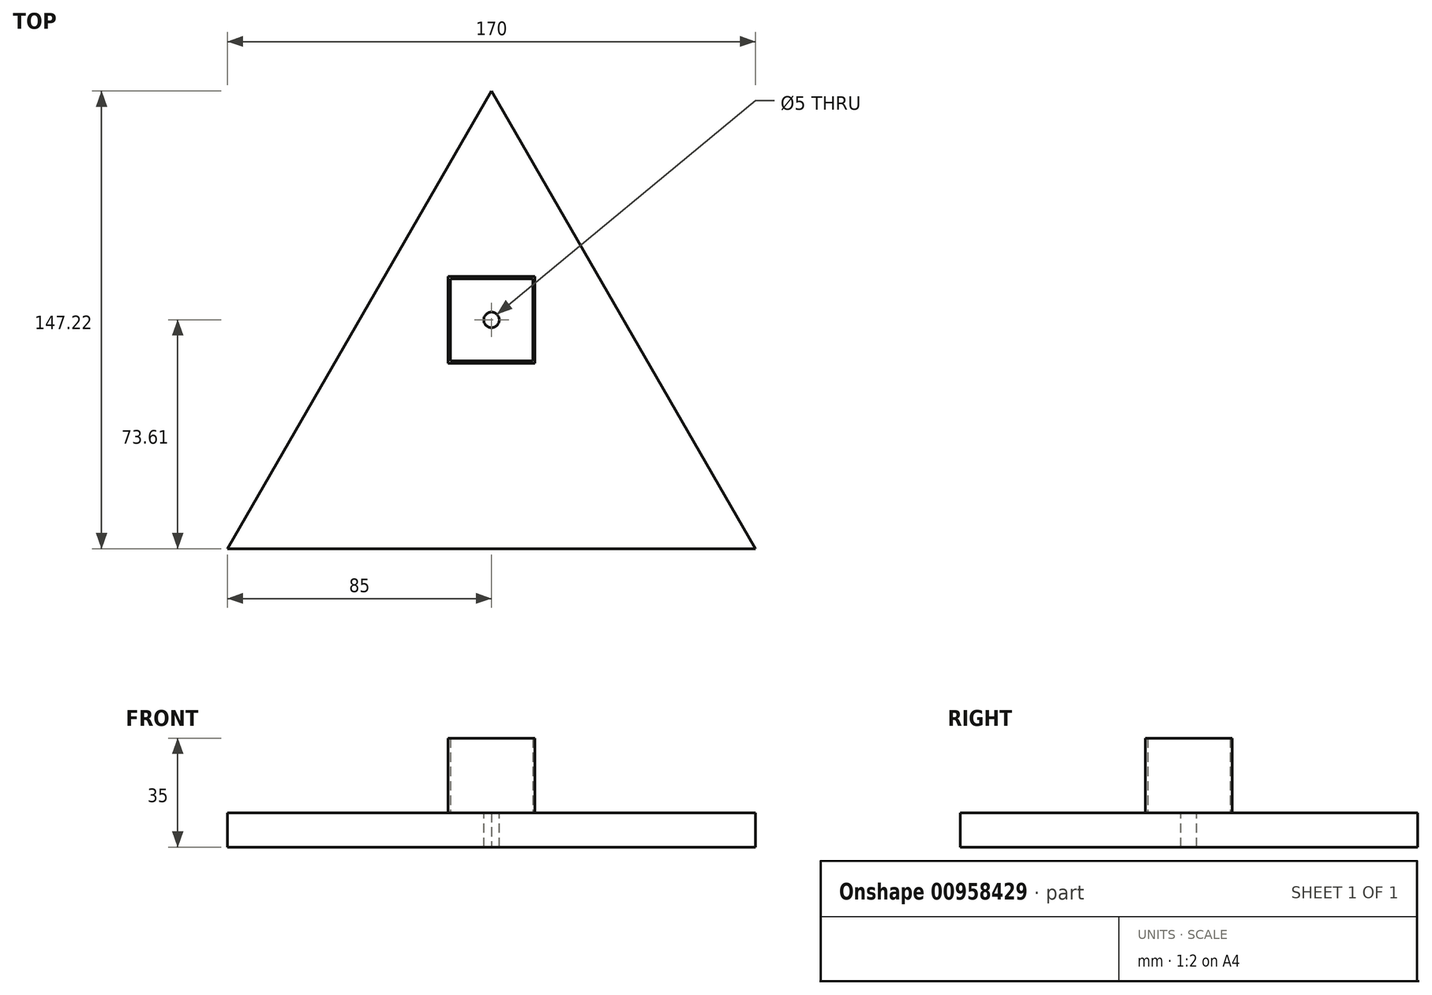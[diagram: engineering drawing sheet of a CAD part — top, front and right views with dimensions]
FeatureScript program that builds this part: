
annotation { "Feature Type Name" : "Feature", "Feature Type Description" : "" }
export const myFeature = defineFeature(function(context is Context, id is Id, definition is map)
    precondition{}
    {
        {
            var Q0;
            Q0=qCreatedBy(makeId("Top.planeOp"),FACE);
            var sketch = newSketch(context, id + "F0", { "sketchPlane" : qUnion([Q0])});
            skLineSegment(sketch, "E0", {"start": v(-85, -73.61) * mm, "end": v(85, -73.61) * mm});
            skLineSegment(sketch, "E1", {"start": v(85, -73.61) * mm, "end": v(0, 73.61) * mm});
            skLineSegment(sketch, "E2", {"start": v(0, 73.61) * mm, "end": v(-85, -73.61) * mm});
            skPoint(sketch, "E3", {"position": v(0, -73.61) * mm});
            skLineSegment(sketch, "E4", {"start": v(0, 73.61) * mm, "end": v(0, -73.61) * mm});
            skPoint(sketch, "E5", {"position": v(0, 0) * mm});
            skPoint(sketch, "E6", {"position": v(-42.5, 0) * mm});
            skPoint(sketch, "E7", {"position": v(42.5, 0) * mm});
            skSolve(sketch);
        }
        {
            var Q0;
            Q0 = qSketchRegion(id + "F0", true);
            extrude(context, id + "F1", {"entities" : qUnion([Q0]), "depth" : 11 * mm, "offsetDistance" : 25 * mm});
        }
        {
            var Q0;
            Q0=makeQuery(id+"F1.opExtrude","CAP_FACE",FACE,{"disambiguationData":[OSD([sQuery(id+"F0.wireOp",EDGE,"E0"),sQuery(id+"F0.wireOp",EDGE,"E1"),sQuery(id+"F0.wireOp",EDGE,"E2")])],"isStart":false});
            var sketch = newSketch(context, id + "F2", { "sketchPlane" : qUnion([Q0])});
            skLineSegment(sketch, "E8.bottom", {"start": v(-13.25, 13.25) * mm, "end": v(13.25, 13.25) * mm});
            skLineSegment(sketch, "E8.top", {"start": v(-13.25, -13.25) * mm, "end": v(13.25, -13.25) * mm});
            skLineSegment(sketch, "E8.left", {"start": v(-13.25, 13.25) * mm, "end": v(-13.25, -13.25) * mm});
            skLineSegment(sketch, "E8.right", {"start": v(13.25, 13.25) * mm, "end": v(13.25, -13.25) * mm});
            skPoint(sketch, "E9", {"position": v(0, 13.25) * mm});
            skPoint(sketch, "E10", {"position": v(-13.25, 0) * mm});
            skSolve(sketch);
        }
        {
            var Q0;
            Q0=makeQuery(id+"F1.opExtrude","CAP_FACE",FACE,{"disambiguationData":[OSD([sQuery(id+"F0.wireOp",EDGE,"E0"),sQuery(id+"F0.wireOp",EDGE,"E1"),sQuery(id+"F0.wireOp",EDGE,"E2")])],"isStart":false});
            var sketch = newSketch(context, id + "F3", { "sketchPlane" : qUnion([Q0])});
            skLineSegment(sketch, "E11.bottom", {"start": v(-14, 14) * mm, "end": v(14, 14) * mm});
            skLineSegment(sketch, "E11.top", {"start": v(-14, -14) * mm, "end": v(14, -14) * mm});
            skLineSegment(sketch, "E11.left", {"start": v(-14, 14) * mm, "end": v(-14, -14) * mm});
            skLineSegment(sketch, "E11.right", {"start": v(14, 14) * mm, "end": v(14, -14) * mm});
            skPoint(sketch, "E12", {"position": v(0, 14) * mm});
            skPoint(sketch, "E13", {"position": v(-14, 0) * mm});
            skSolve(sketch);
        }
        {
            var Q0;
            Q0 = qSketchRegion(id + "F3", true);
            extrude(context, id + "F4", {"entities" : qUnion([Q0]), "operationType" : NewBodyOperationType.ADD, "depth" : 24 * mm, "offsetDistance" : 25 * mm});
        }
        {
            var Q0;
            Q0 = qSketchRegion(id + "F2", true);
            extrude(context, id + "F5", {"entities" : qUnion([Q0]), "operationType" : NewBodyOperationType.REMOVE, "depth" : 24 * mm, "offsetDistance" : 25 * mm});
        }
        {
            var Q0;
            Q0=makeQuery(id+"F2.imprint","IMPRINT",FACE,{"disambiguationData":[TD([[makeQuery(id+"F2.imprint","IMPRINT",EDGE,{"derivedFrom":sQuery(id+"F2.wireOp",EDGE,"E8.bottom")}),1.0]])]});
            var sketch = newSketch(context, id + "F6", { "sketchPlane" : qUnion([Q0])});
            skCircle(sketch, "E14", {"center": v(0, 0) * mm, "radius": 2.5 * mm});
            skSolve(sketch);
        }
        {
            var Q0;
            Q0 = qSketchRegion(id + "F6", true);
            extrude(context, id + "F7", {"entities" : qUnion([Q0]), "operationType" : NewBodyOperationType.REMOVE, "oppositeDirection" : true, "depth" : 25 * mm, "offsetDistance" : 25 * mm});
        }
    });
